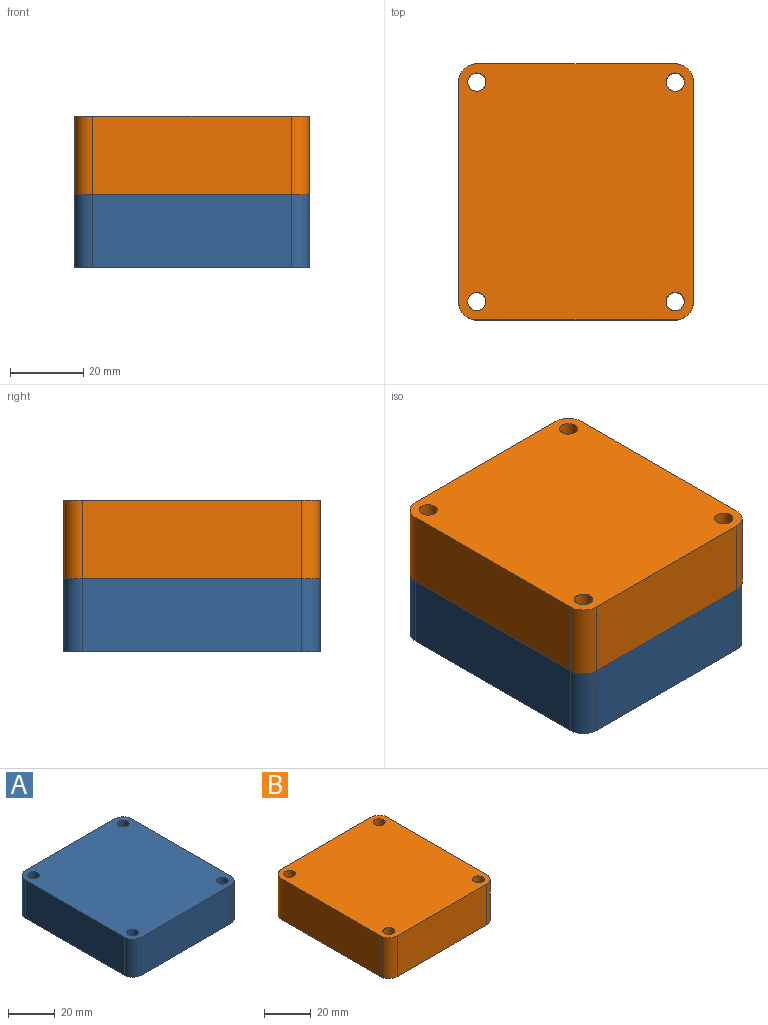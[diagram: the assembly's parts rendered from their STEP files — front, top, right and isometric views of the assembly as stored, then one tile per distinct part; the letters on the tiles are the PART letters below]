
ASSEMBLY  parts=2 mates=1
PART A: 45 faces, bbox 64.3x70.1x55.3 mm
  f0: plane 54.24x20mm, normal (0,1,0), area 1015.6mm2, adj f1,f9,f40,f41,f44
  f1: plane 70x64.24mm, normal (0,0,-1), area 2501.6mm2, adj f0,f2,f3,f4,f5,f6,f7,f8
  f2: plane 54.24x20mm, normal (0,-1,0), area 1084.8mm2, adj f1,f9,f39,f42
  f3: plane 60x20mm, normal (1,0,0), area 1200mm2, adj f1,f9,f39,f40
  f4: cylinder r=2.5mm len=20mm, axis (0,0,-1), area 314.2mm2, adj f1,f9
  f5: cylinder r=2.5mm len=20mm, axis (0,0,-1), area 314.2mm2, adj f1,f9
  f6: cylinder r=2.5mm len=20mm, axis (0,0,-1), area 314.2mm2, adj f1,f9
  f7: cylinder r=2.5mm len=20mm, axis (0,0,-1), area 314.2mm2, adj f1,f9
  f8: plane 60x20mm, normal (-1,0,0), area 1200mm2, adj f1,f9,f41,f42
  f9: plane 70x64.24mm, normal (0,0,1), area 4396.7mm2, adj f0,f2,f3,f4,f5,f6,f7,f8
  f10: cylinder r=18.68mm len=37.37mm, axis (0,0,-1), area 57.6mm2, adj f11,f17,f37,f38
  f11: torus R=41.07mm, axis (1,0,0), area 44.3mm2, adj f10,f12,f37,f38
  f12: cylinder r=18.28mm len=36.56mm, axis (0,0,-1), area 58.3mm2, adj f11,f17,f37,f38
  f13: bspline ~1.86x1.37mm, area 3.2mm2, adj f14,f15,f32,f36
  f14: bspline ~4.95x2.59mm, area 12.5mm2, adj f13,f17,f22,f31,f36
  f15: bspline ~4.95x2.59mm, area 12.5mm2, adj f13,f17,f23,f33,f36
  f16: cylinder r=25.25mm len=15.11mm, axis (0,0,1), area 17.8mm2, adj f1,f24,f34,f35
  f17: torus R=41.07mm, axis (1,0,0), area 1521.5mm2, adj f10,f12,f14,f15,f20,f21,f22,f23
  f18: bspline ~1.84x1.55mm, area 1.3mm2, adj f25,f26,f44
  f19: bspline ~1.84x1.55mm, area 1.3mm2, adj f20,f27,f44
  f20: bspline ~19.4x16.19mm, area 64.8mm2, adj f17,f19,f21,f28,f44
  f21: bspline ~15.11x2.5mm, area 38.2mm2, adj f17,f20,f22,f29
  f22: bspline ~19.4x16.19mm, area 64.9mm2, adj f14,f17,f21,f30
  f23: bspline ~19.4x16.19mm, area 64.9mm2, adj f15,f17,f24,f34
  f24: bspline ~15.11x2.49mm, area 38.2mm2, adj f16,f17,f23,f25
  f25: bspline ~19.41x16.2mm, area 64.8mm2, adj f17,f18,f24,f35,f44
  f26: cylinder r=10.1mm len=1.8mm, axis (0,0,1), area 1.9mm2, adj f1,f18,f35,f44
  f27: cylinder r=10.1mm len=1.8mm, axis (0,0,1), area 1.9mm2, adj f1,f19,f28,f44
  f28: cylinder r=33.05mm len=18.92mm, axis (0,0,1), area 30.1mm2, adj f1,f20,f27,f29
  f29: cylinder r=25.25mm len=15.11mm, axis (0,0,1), area 18.6mm2, adj f1,f21,f28,f30
  f30: cylinder r=33.05mm len=18.92mm, axis (0,0,1), area 30.1mm2, adj f1,f22,f29,f31
  f31: cylinder r=10.1mm len=4.95mm, axis (0,0,1), area 6mm2, adj f1,f14,f30,f32
  f32: plane 1.34x1.12mm, normal (0,1,0), area 1.5mm2, adj f1,f13,f31,f33
  f33: cylinder r=10.1mm len=4.95mm, axis (0,0,1), area 6mm2, adj f1,f15,f32,f34
  f34: cylinder r=33.05mm len=18.92mm, axis (0,0,1), area 30.1mm2, adj f1,f16,f23,f33
  f35: cylinder r=33.05mm len=18.92mm, axis (0,0,1), area 30.1mm2, adj f1,f16,f25,f26
  f36: cone r=6.4mm half-angle=14deg, axis (0,0,1), area 0.5mm2, adj f13,f14,f15,f17
  f37: cone r=6.4mm half-angle=14deg, axis (0,0,1), area 0.4mm2, adj f10,f11,f12,f17
  f38: cone r=6.4mm half-angle=14deg, axis (0,0,1), area 0.4mm2, adj f10,f11,f12,f17
  f39: cylinder r=5mm len=20mm, axis (0,0,1), area 157.1mm2, adj f1,f2,f3,f9
  f40: cylinder r=5mm len=20mm, axis (0,0,-1), area 157.1mm2, adj f0,f1,f3,f9
  f41: cylinder r=5mm len=20mm, axis (0,0,1), area 157.1mm2, adj f0,f1,f8,f9
  f42: cylinder r=5mm len=20mm, axis (0,0,-1), area 157.1mm2, adj f1,f2,f8,f9
  f43: plane 9.74x3.78mm, normal (0,1,0), area 25.3mm2, adj f17,f44
  f44: cylinder r=5mm len=16.8mm, axis (0,1,0), area 316.9mm2, adj f0,f1,f17,f18,f19,f20,f25,f26
PART B: 45 faces, bbox 64.2x70x55.3 mm
  f0: cylinder r=18.68mm len=37.37mm, axis (0,0,-1), area 57.6mm2, adj f1,f7,f29,f30
  f1: torus R=41.07mm, axis (1,0,0), area 44.3mm2, adj f0,f2,f29,f30
  f2: cylinder r=18.28mm len=36.56mm, axis (0,0,-1), area 58.3mm2, adj f1,f7,f29,f30
  f3: bspline ~1.86x1.37mm, area 3.2mm2, adj f4,f5,f24,f28
  f4: bspline ~4.95x2.59mm, area 12.5mm2, adj f3,f7,f13,f23,f28
  f5: bspline ~4.95x2.59mm, area 12.5mm2, adj f3,f7,f14,f25,f28
  f6: cylinder r=25.25mm len=15.11mm, axis (0,0,1), area 39.3mm2, adj f15,f26,f27,f31
  f7: torus R=41.07mm, axis (1,0,0), area 1593.9mm2, adj f0,f2,f4,f5,f8,f9,f10,f11
  f8: bspline ~1.96x1.53mm, area 3.6mm2, adj f7,f9,f10,f18
  f9: bspline ~4.95x2.59mm, area 12.9mm2, adj f7,f8,f16,f17
  f10: bspline ~4.95x2.59mm, area 12.9mm2, adj f7,f8,f11,f19
  f11: bspline ~19.4x16.19mm, area 64.9mm2, adj f7,f10,f12,f20
  f12: bspline ~15.11x2.5mm, area 38.2mm2, adj f7,f11,f13,f21
  f13: bspline ~19.4x16.19mm, area 64.9mm2, adj f4,f7,f12,f22
  f14: bspline ~19.4x16.19mm, area 64.9mm2, adj f5,f7,f15,f26
  f15: bspline ~15.11x2.49mm, area 38.2mm2, adj f6,f7,f14,f16
  f16: bspline ~19.41x16.2mm, area 64.9mm2, adj f7,f9,f15,f27
  f17: cylinder r=10.1mm len=4.95mm, axis (0,0,1), area 13.2mm2, adj f9,f18,f27,f31
  f18: plane 2.52x1.34mm, normal (0,-1,0), area 3.4mm2, adj f8,f17,f19,f31
  f19: cylinder r=10.1mm len=4.95mm, axis (0,0,1), area 13.2mm2, adj f10,f18,f20,f31
  f20: cylinder r=33.05mm len=18.92mm, axis (0,0,1), area 65mm2, adj f11,f19,f21,f31
  f21: cylinder r=25.25mm len=15.11mm, axis (0,0,1), area 40mm2, adj f12,f20,f22,f31
  f22: cylinder r=33.05mm len=18.92mm, axis (0,0,1), area 65mm2, adj f13,f21,f23,f31
  f23: cylinder r=10.1mm len=4.95mm, axis (0,0,1), area 13.2mm2, adj f4,f22,f24,f31
  f24: plane 2.52x1.34mm, normal (0,1,0), area 3.4mm2, adj f3,f23,f25,f31
  f25: cylinder r=10.1mm len=4.95mm, axis (0,0,1), area 13.2mm2, adj f5,f24,f26,f31
  f26: cylinder r=33.05mm len=18.92mm, axis (0,0,1), area 65mm2, adj f6,f14,f25,f31
  f27: cylinder r=33.05mm len=18.92mm, axis (0,0,1), area 65mm2, adj f6,f16,f17,f31
  f28: cone r=6.4mm half-angle=14deg, axis (0,0,1), area 0.5mm2, adj f3,f4,f5,f7
  f29: cone r=6.4mm half-angle=14deg, axis (0,0,1), area 0.4mm2, adj f0,f1,f2,f7
  f30: cone r=6.4mm half-angle=14deg, axis (0,0,1), area 0.4mm2, adj f0,f1,f2,f7
  f31: plane 70x64.24mm, normal (0,0,-1), area 2560.7mm2, adj f6,f17,f18,f19,f20,f21,f22,f23
  f32: cylinder r=5mm len=21.4mm, axis (0,0,-1), area 168.1mm2, adj f31,f33,f39,f43
  f33: plane 54.24x21.4mm, normal (0,1,0), area 1160.7mm2, adj f31,f32,f34,f43
  f34: cylinder r=5mm len=21.4mm, axis (0,0,1), area 168.1mm2, adj f31,f33,f35,f43
  f35: plane 60x21.4mm, normal (-1,0,0), area 1284mm2, adj f31,f34,f36,f43
  f36: cylinder r=5mm len=21.4mm, axis (0,0,-1), area 168.1mm2, adj f31,f35,f37,f43
  f37: plane 54.24x21.4mm, normal (0,-1,0), area 1160.7mm2, adj f31,f36,f38,f43
  f38: cylinder r=5mm len=21.4mm, axis (0,0,1), area 168.1mm2, adj f31,f37,f39,f43
  f39: plane 60x21.4mm, normal (1,0,0), area 1284mm2, adj f31,f32,f38,f43
  f40: cylinder r=2.5mm len=21.4mm, axis (0,0,-1), area 336.2mm2, adj f31,f43
  f41: cylinder r=2.5mm len=21.4mm, axis (0,0,-1), area 336.2mm2, adj f31,f43
  f42: cylinder r=2.5mm len=21.4mm, axis (0,0,-1), area 336.2mm2, adj f31,f43
  f43: plane 70x64.24mm, normal (0,0,1), area 4396.7mm2, adj f32,f33,f34,f35,f36,f37,f38,f39
  f44: cylinder r=2.5mm len=21.4mm, axis (0,0,-1), area 336.2mm2, adj f31,f43
PLACE A rot(axis=(0,1,0),180deg) t=(-1.29,15.92,-36.13)mm
PLACE B t=(-31.42,-19.08,-34.73)mm
MATE slider A.f7 <-> B.f32  axis (0,0,1) through (-6.23,10.92,-36.13)mm
